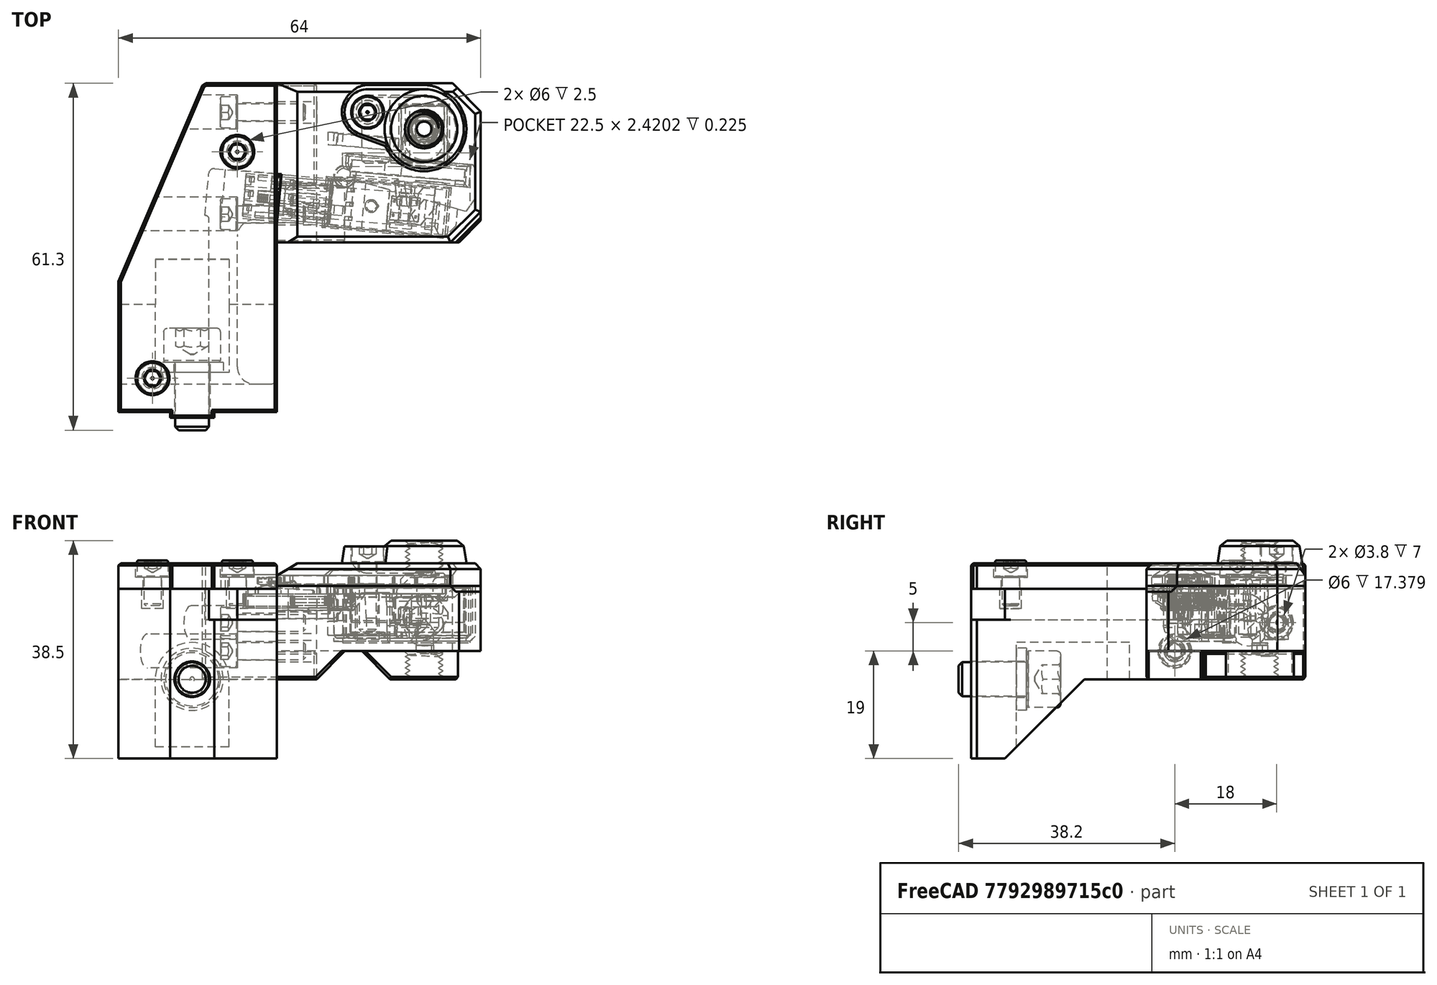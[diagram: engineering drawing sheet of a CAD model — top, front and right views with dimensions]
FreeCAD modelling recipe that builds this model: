
FCSTD DOCUMENT  (FreeCAD 0.19R24291 (Git))
Label: filament-sensor-assembly
License: Other
LicenseURL: GPL3
objects: Part::Feature×9, Part::FeaturePython×7, App::Part×1
note: 16 computed .brp shape members not serialized (recipe doc carries the construction recipe); baked Part::Feature solids carry a one-line shape summary decoded from their .brp

FEATURE [Part::Feature] Cut008004003004014002002005003004003002003021020001  label="Cut008004003004014002002005003004003002003021024"
  shape: bbox 35 x 59.1 x 30 mm, 60 faces (baked)
FEATURE [Part::Feature] Chamfer004013007011015006009007008  label="Chamfer012"
  shape: bbox 36.01 x 28.11 x 18.46 mm, 152 faces (baked)
FEATURE [Part::Feature] Part__Feature043001  label="magnet_20x6x2 v002"
  shape: bbox 20.1 x 3.736 x 6 mm, 6 faces (baked)
FEATURE [Part::Feature] Part__Feature032001  label="fs_lever001"
  shape: bbox 24.12 x 9.285 x 8.809 mm, 52 faces (baked)
FEATURE [Part::Feature] Part__Feature044001  label="magnet_10x6x2 v002"
  shape: bbox 10.14 x 2.864 x 6 mm, 6 faces (baked)
FEATURE [Part::Feature] Fusion001001  label="Fusion002011011013004002017"
  shape: bbox 36.02 x 10.86 x 8.121 mm, 301 faces (baked)
FEATURE [Part::Feature] Chamfer005001  label="Chamfer011"
  shape: bbox 36 x 28.1 x 8.302 mm, 88 faces (baked)
FEATURE [Part::Feature] Part__Feature045001  label="steel_ball v002"
  shape: bbox 7 x 7 x 7 mm, 1 faces (baked)
FEATURE [Part::FeaturePython] Screw  label="M3x12-Screw001"  # Fasteners workbench fastener (typed FeaturePython)
  Placement = pos=(-7,9,10) rot=(0,-1,0;1.5708rad)
  baseObject = -> Cut008004003004014002002005003004003002003021020001 [Edge81]
  diameter = 4
  invert = false
  length = 4
  lengthCustom = 12
  matchOuter = true
  offset = 0
  thread = false
  type = 33
FEATURE [Part::FeaturePython] Screw001  label="M3x12-Screw"  # Fasteners workbench fastener (typed FeaturePython)
  Placement = pos=(-7,-9,5) rot=(0,-1,0;1.5708rad)
  baseObject = -> Cut008004003004014002002005003004003002003021020001 [Edge78]
  diameter = 4
  invert = false
  length = 4
  lengthCustom = 12
  matchOuter = true
  offset = 0
  thread = false
  type = 33
FEATURE [Part::FeaturePython] Screw004  label="M3x12-Screw002"  # Fasteners workbench fastener (typed FeaturePython)
  Placement = pos=(16,8.995,20.5) rot=(0,0,1;0rad)
  baseObject = -> Chamfer005001 [Edge135]
  diameter = 4
  invert = true
  length = 4
  lengthCustom = 12
  matchOuter = true
  offset = 0
  thread = false
  type = 33
FEATURE [Part::FeaturePython] Washer  label="M6-Washer"  # Fasteners workbench fastener (typed FeaturePython)
  Placement = pos=(-15,-37,4e-15) rot=(-1,0,0;1.5708rad)
  baseObject = -> Cut008004003004014002002005003004003002003021020001 [Edge16]
  diameter = 7
  invert = true
  matchOuter = true
  offset = 0
  type = 5
FEATURE [Part::FeaturePython] Screw005  label="M6x12-Screw"  # Fasteners workbench fastener (typed FeaturePython)
  Placement = pos=(-15,-35.2,4.4e-15) rot=(-1,0,0;1.5708rad)
  baseObject = -> Washer [Edge1]
  diameter = 7
  invert = false
  length = 14
  lengthCustom = 12
  matchOuter = true
  offset = 0
  thread = false
  type = 33
FEATURE [Part::Feature] Cut008004003004014002002005003004003002003021022001002001001
  shape: bbox 28 x 59.1 x 4.5 mm, 36 faces (baked)
FEATURE [Part::FeaturePython] Screw006  label="M3x5-Screw"  # Fasteners workbench fastener (typed FeaturePython)
  Placement = pos=(-7,2,18) rot=(0,0,1;0rad)
  baseObject = -> Cut008004003004014002002005003004003002003021022001002001001 [Edge2]
  diameter = 4
  invert = false
  length = 0
  lengthCustom = 5
  matchOuter = true
  offset = 0
  thread = false
  type = 33
FEATURE [Part::FeaturePython] Screw007  label="M3x5-Screw001"  # Fasteners workbench fastener (typed FeaturePython)
  Placement = pos=(-22,-38,18) rot=(0,0,1;0rad)
  baseObject = -> Cut008004003004014002002005003004003002003021022001002001001 [Edge6]
  diameter = 4
  invert = false
  length = 0
  lengthCustom = 5
  matchOuter = true
  offset = 0
  thread = false
  type = 33
FEATURE [App::Part] Part067  label="filament-sensor"
  Group = -> [Chamfer004013007011015006009007008,Chamfer005001,Cut008004003004014002002005003004003002003021020001,Part__Feature032001,Part__Feature043001,Part__Feature044001,Part__Feature045001,Fusion001001,Screw001,Screw,Screw004,Washer,Screw005,Cut008004003004014002002005003004003002003021022001002001001,Screw007,Screw006]
  Origin = -> Origin069
  Placement = pos=(156,296,198) rot=(0,0,-1;3.14159rad)
